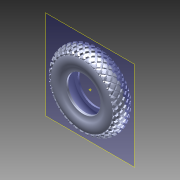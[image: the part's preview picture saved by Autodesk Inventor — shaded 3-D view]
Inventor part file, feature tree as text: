
AUTODESK INVENTOR PART (.ipt)
format: ipt  version: 2013 (Build 170138000, 138)  size: 11,052,032 bytes
history: native  units: in
note: dims shown in document units (in); Inventor stores cm internally (conversion verified against a paired STEP export)
features: pattern_circular x1, imported_body x1, plane x1, other x1
ambient origin geometry x8: Origin, YZ Plane, XZ Plane, XY Plane, X Axis, Y Axis, Z Axis, Center Point
feature tree (4):
  pattern_circular  "CirPattern1"
  imported_body  "Base1"
  plane  "Work Plane1"
  other  "Work Point1"
